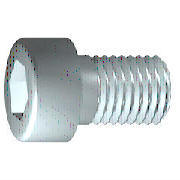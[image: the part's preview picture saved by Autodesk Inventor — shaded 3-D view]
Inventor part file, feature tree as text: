
AUTODESK INVENTOR PART (.ipt)
format: ipt  version: 2023.3 (Build 273359000, 359)  size: 193,024 bytes
history: native  units: mm (DEFAULTED — no unit token found)
features: sketch x2, other x1, extrude x1, plane x1, fillet x1
ambient origin geometry x7: Origin, YZ Plane, XY Plane, X Axis, Y Axis, Z Axis, Center Point
bodies: Solid1 (feature_tree)
feature tree (6):
  other  "Körper"
  extrude  "Loch"  Depth=1.6mm
  plane  "Work Plane1"
  fillet  "Fillet2"  Radius=1.6mm
  sketch  "Skizze1"  dims[d1=5.125mm d2=0.214807mm d3=1.6mm]
  sketch  "Skizze2"  dims[d4=0.7mm d5=60.0deg d6=1.6mm d7=1.6mm d8=1.732051mm d9=3.0mm d10=90.0deg d11=10.0mm d12=0.0mm d13=5.125mm d14=0.0mm d15=0.214707mm d16=0.214707mm d17=0.16mm d19=0.0mm d26=6.0mm d27=45.0deg d28=0.0mm d29=0.0mm d30=0.1mm]
